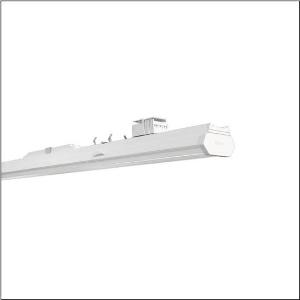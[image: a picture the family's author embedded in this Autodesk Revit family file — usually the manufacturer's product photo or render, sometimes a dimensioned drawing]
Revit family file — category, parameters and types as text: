
# Revit family: licross_r__11_protected_ho_51td1bdn4e5m3s4_89af
name_source: partatom
category: Lighting Fixtures
units: mm (PartAtom-declared; Revit-internal decimal feet)

## family parameters
Cut with Voids When Loaded = No
Host = Face
Light Source = No
Part Type = Normal
Room Calculation Point = No
Round Connector Dimension = Use Diameter
Shared = No

## types (1)
- --- (1 x LED, 920 lm, 7.4 W, 4000K)
    Apparent Load = 7 VA
    CIE Flux Codes = 54 82 95 97 100
    Color Rendering = 80
    Color Temperature = 4000K
    Default Elevation = 1800 mm
    Description = Licross® 11 Protected HO, luminaire insert, of sheet steel, galvanised, coil coated, white, length: 1.500mm, width: 90mm, height: 101mm, LED rated luminous flux: 14.500lm, light colour: 840, control gear: DALI 2, with plug, 6-pole, with phase selection, for trunking rail, 9 or 11-core, mains connection: 220..240V, AC, 50/60Hz, rated input power: 91W, for trunking rail, 9-/11-core, halogen-free wiring, for emergency light function, converter,control gear: single battery element, battery: LiFePO4, 9Ah, primary optical cover: cover, of PMMA, light emission: direct distribution, primary light characteristic: symmetric, protection rating (complete): IP54, insulation class (complete): insulation class I (protective earthing), certification: CE, UKCA, protection symbol: D if used in an environment with non-conductive dust loads with corresponding accessories, impact resistance: IK06, permissible ambient temperature for indoor applications: +5..+30°C, standard: EN 60598-2-22, LABS conformity tested according to VDMA 24364:2018-05, reducing of maximum allowable ambient temperature of 5°C with ceiling mounting, corresponds to IFS (International Featured Standards) requirements for safety and quality in the food industry, packaging unit: 1 piece
    Height = 92 mm
    Lamp = 1 x LED
    Lamp Light Flux = 920 lm
    Lamp Power = 7.4 W
    Lamp count = 1
    Length = 1500 mm
    Luminous efficacy = 124 lm/W
    Manufacturer = Siteco
    ModVariant = No
    Model = 51TD1BDN4E5M3S4
    Mounting Place = Ceiling
    Mounting Type = Pendant
    Number of Poles = 1
    OnlyDefault = Yes
    Power Factor = 1
    Product Name = Licross® 11 Protected HO
    Product group = luminaire insert
    ProductGroupID = 901
    Protection Class = Protection class I
    Protection Degree = IP 54
    RLX_Detail_Level = 1
    RLX_Emergency_Light_Flux = 0 lm
    RLX_Emergency_Type = 0
    RLX_Emergency_Type_DB = No
    RlxData = <blob elided: 24821 chars, md5=ddf5ecad>
    Socket = socket
    Standby Power = 0 W
    System Light Flux = 920 lm
    System Power = 7 W
    Type Comments = : emergency light operation: 3 h
    Type Image = l_1256145.jpg
    URL = http://relux.com
    VarID = @adj_060015
    Voltage = 0 V
    Weight = 0.00 kg
    Width = 88 mm

## geometry (parser evidence)
native form markers: Blend x4, Sweep x10
no freeform markers — native parametric forms only
